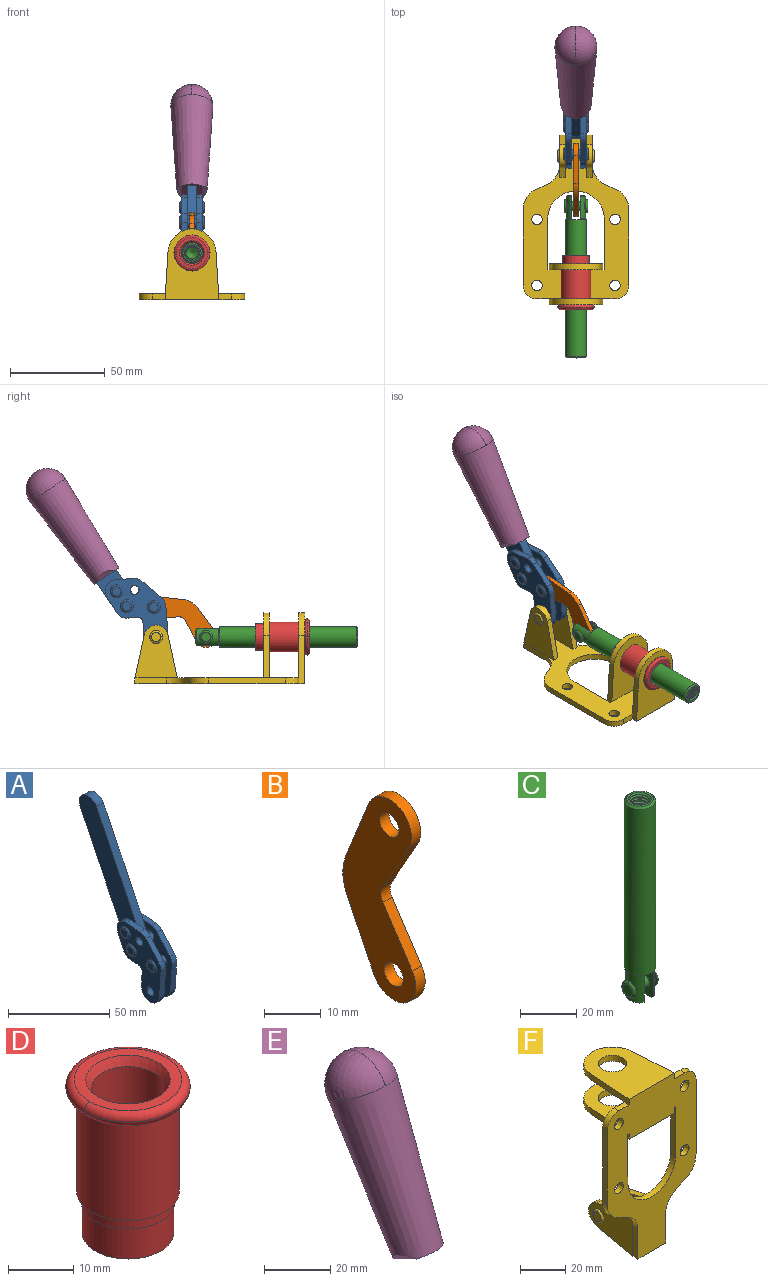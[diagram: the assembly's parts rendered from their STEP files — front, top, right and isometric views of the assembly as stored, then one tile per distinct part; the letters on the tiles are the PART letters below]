
ASSEMBLY  parts=6 mates=6
PART A: 59 faces, bbox 12.9x60.2x99.6 mm
  f0: torus R=2.39mm, axis (-1,0,0), area 14.9mm2, adj f20,f43,f51
  f1: torus R=2.39mm, axis (-1,0,0), area 14.9mm2, adj f19,f42,f51
  f2: torus R=2.39mm, axis (-1,0,0), area 14.9mm2, adj f18,f35,f51
  f3: torus R=2.39mm, axis (-1,0,0), area 14.9mm2, adj f14,f17,f23
  f4: torus R=2.39mm, axis (-1,0,0), area 14.9mm2, adj f13,f16,f23
  f5: torus R=2.39mm, axis (-1,0,0), area 14.9mm2, adj f12,f15,f23
  f6: cylinder r=2.39mm len=4.78mm, axis (1,0,0), area 46.5mm2, adj f48,f50,f51
  f7: cylinder r=2.39mm len=4.78mm, axis (1,0,0), area 46.5mm2, adj f50,f51
  f8: cylinder r=6.35mm len=12.68mm, axis (1,0,0), area 61.8mm2, adj f38,f39,f50,f51
  f9: cylinder r=2.39mm len=4.78mm, axis (-1,0,0), area 70.5mm2, adj f46,f50
  f10: cylinder r=2.39mm len=4.78mm, axis (-1,0,0), area 46.5mm2, adj f23,f45,f46
  f11: cylinder r=2.39mm len=4.78mm, axis (-1,0,0), area 46.5mm2, adj f23,f46
  f12: plane 4.78x4.78mm, normal (1,0,0), area 17.9mm2, adj f5,f15
  f13: plane 4.78x4.78mm, normal (1,0,0), area 17.9mm2, adj f4,f16
  f14: plane 4.78x4.78mm, normal (1,0,0), area 17.9mm2, adj f3,f17
  f15: torus R=2.39mm, axis (-1,0,0), area 14.9mm2, adj f5,f12,f23
  f16: torus R=2.39mm, axis (-1,0,0), area 14.9mm2, adj f4,f13,f23
  f17: torus R=2.39mm, axis (-1,0,0), area 14.9mm2, adj f3,f14,f23
  f18: plane 4.78x4.78mm, normal (-1,0,0), area 17.9mm2, adj f2,f35
  f19: plane 4.78x4.78mm, normal (-1,0,0), area 17.9mm2, adj f1,f42
  f20: plane 4.78x4.78mm, normal (-1,0,0), area 17.9mm2, adj f0,f43
  f21: plane 2.26x0.2mm, normal (1,0,0), area 0.2mm2, adj f31,f44
  f22: plane 2.26x0.2mm, normal (-1,0,0), area 0.2mm2, adj f41,f44
  f23: plane 39.37x30.77mm, normal (1,0,0), area 565.5mm2, adj f3,f4,f5,f10,f11,f15,f16,f17
  f24: cylinder r=6.1mm len=4.15mm, axis (-1,0,0), area 14.7mm2, adj f23,f25,f32,f46
  f25: plane 10.25x9.01mm, normal (0,-0.75,0.66), area 42.3mm2, adj f23,f24,f26,f46
  f26: cylinder r=6.35mm len=4.64mm, axis (-1,0,0), area 15.6mm2, adj f23,f25,f27,f46
  f27: plane 15.84x3.1mm, normal (0,-1,-0.07), area 49.2mm2, adj f23,f26,f28,f46
  f28: cylinder r=6.35mm len=12.68mm, axis (-1,0,0), area 61.8mm2, adj f23,f27,f29,f46
  f29: plane 8.11x3.1mm, normal (0,1,0.07), area 25.2mm2, adj f23,f28,f30,f46
  f30: cylinder r=3.05mm len=3.25mm, axis (-1,0,0), area 14.8mm2, adj f23,f29,f31,f46
  f31: plane 5.99x3.1mm, normal (0,0.07,-1), area 18.6mm2, adj f21,f23,f30,f44,f46
  f32: plane 9.5x3.1mm, normal (0,-0.07,1), area 29.5mm2, adj f23,f24,f33,f46,f47
  f33: cylinder r=6.1mm len=8.63mm, axis (-1,0,0), area 39.1mm2, adj f23,f32,f34,f47
  f34: plane 8.65x3.96mm, normal (0,0.91,-0.42), area 29.5mm2, adj f23,f33,f44,f47
  f35: torus R=2.39mm, axis (-1,0,0), area 14.9mm2, adj f2,f18,f51
  f36: plane 10.25x9.01mm, normal (0,-0.75,0.66), area 42.3mm2, adj f37,f49,f50,f51
  f37: cylinder r=6.35mm len=4.64mm, axis (1,0,0), area 15.6mm2, adj f36,f38,f50,f51
  f38: plane 15.84x3.1mm, normal (0,-1,-0.07), area 49.2mm2, adj f8,f37,f50,f51
  f39: plane 8.11x3.1mm, normal (0,1,0.07), area 25.2mm2, adj f8,f40,f50,f51
  f40: cylinder r=3.05mm len=3.25mm, axis (1,0,0), area 14.8mm2, adj f39,f41,f50,f51
  f41: plane 5.99x3.1mm, normal (0,0.07,-1), area 18.6mm2, adj f22,f40,f44,f50,f51
  f42: torus R=2.39mm, axis (-1,0,0), area 14.9mm2, adj f1,f19,f51
  f43: torus R=2.39mm, axis (-1,0,0), area 14.9mm2, adj f0,f20,f51
  f44: cylinder r=6.35mm len=12.12mm, axis (-1,0,0), area 128.9mm2, adj f21,f22,f23,f31,f34,f41,f46,f47
  f45: plane 2.65x1.35mm, normal (1,0,0), area 1mm2, adj f10,f55
  f46: plane 39.08x20.42mm, normal (-1,0,0), area 412.5mm2, adj f9,f10,f11,f24,f25,f26,f27,f28
  f47: plane 77.62x39.82mm, normal (1,0,0), area 850mm2, adj f32,f33,f34,f44,f53,f54,f55
  f48: plane 2.65x1.35mm, normal (-1,0,0), area 1mm2, adj f6,f55
  f49: cylinder r=6.1mm len=4.15mm, axis (1,0,0), area 14.7mm2, adj f36,f50,f51,f56
  f50: plane 39.08x20.42mm, normal (1,0,0), area 412.5mm2, adj f6,f7,f8,f9,f36,f37,f38,f39
  f51: plane 39.37x30.77mm, normal (-1,0,0), area 565.5mm2, adj f0,f1,f2,f6,f7,f8,f35,f36
  f52: plane 8.65x3.96mm, normal (0,0.91,-0.42), area 29.5mm2, adj f44,f51,f57,f58
  f53: plane 68.49x33.4mm, normal (0,0.9,-0.44), area 358.1mm2, adj f44,f47,f54,f58
  f54: cylinder r=6.35mm len=12.06mm, axis (1,0,0), area 93.7mm2, adj f47,f53,f55,f58
  f55: plane 68.49x33.4mm, normal (0,-0.9,0.44), area 358.1mm2, adj f44,f45,f46,f47,f48,f50,f54,f58
  f56: plane 9.5x3.1mm, normal (0,-0.07,1), area 29.5mm2, adj f49,f50,f51,f57,f58
  f57: cylinder r=6.1mm len=8.63mm, axis (1,0,0), area 39.1mm2, adj f51,f52,f56,f58
  f58: plane 77.62x39.82mm, normal (-1,0,0), area 850mm2, adj f44,f52,f53,f54,f55,f56,f57
PART B: 12 faces, bbox 2.3x18.2x42.8 mm
  f0: cylinder r=2.4mm len=4.8mm, axis (1,0,0), area 34.9mm2, adj f4,f11
  f1: cylinder r=10.41mm len=8.47mm, axis (1,0,0), area 20.2mm2, adj f4,f9,f10,f11
  f2: cylinder r=3.05mm len=3.16mm, axis (1,0,0), area 7.7mm2, adj f4,f6,f7,f11
  f3: cylinder r=2.4mm len=4.8mm, axis (1,0,0), area 34.9mm2, adj f4,f11
  f4: plane 42.81x18.23mm, normal (-1,0,0), area 414.1mm2, adj f0,f1,f2,f3,f5,f6,f7,f8
  f5: cylinder r=5.54mm len=10.67mm, axis (1,0,0), area 41.8mm2, adj f4,f6,f10,f11
  f6: plane 11.66x6.53mm, normal (0,-0.87,-0.49), area 30.9mm2, adj f2,f4,f5,f11
  f7: plane 11.17x7.33mm, normal (0,-0.84,0.55), area 30.9mm2, adj f2,f4,f8,f11
  f8: cylinder r=5.54mm len=10.51mm, axis (1,0,0), area 41.8mm2, adj f4,f7,f9,f11
  f9: plane 13.67x6.67mm, normal (0,0.9,-0.44), area 35.1mm2, adj f1,f4,f8,f11
  f10: plane 14.1x5.7mm, normal (0,0.93,0.37), area 35.1mm2, adj f1,f4,f5,f11
  f11: plane 42.81x18.23mm, normal (1,0,0), area 414.1mm2, adj f0,f1,f2,f3,f5,f6,f7,f8
PART C: 48 faces, bbox 12.6x11.1x86.1 mm
  f0: torus R=2.41mm, axis (-1,0,0), area 15mm2, adj f30,f32,f34
  f1: torus R=2.41mm, axis (-1,0,0), area 15mm2, adj f29,f31,f33
  f2: cylinder r=5.54mm len=72.39mm, axis (0,0,1), area 2518.5mm2, adj f3,f4,f42,f43
  f3: cone r=5.54mm half-angle=45deg, axis (0,0,1), area 7.6mm2, adj f2,f5,f41
  f4: cone r=5.54mm half-angle=45deg, axis (0,0,-1), area 34.9mm2, adj f2,f39
  f5: cylinder r=5.08mm len=11.48mm, axis (0,0,1), area 108.3mm2, adj f3,f7,f8,f41
  f6: cylinder r=2.41mm len=4.83mm, axis (-1,0,0), area 71.2mm2, adj f40,f41
  f7: cylinder r=2.41mm len=4.83mm, axis (-1,0,0), area 7.6mm2, adj f5,f34
  f8: cone r=5.08mm half-angle=45deg, axis (0,0,1), area 10.6mm2, adj f5,f37,f41
  f9: cone r=3.98mm half-angle=45deg, axis (0,0,1), area 17.6mm2, adj f27,f39,f45,f46,f47
  f10: cylinder r=2.41mm len=4.83mm, axis (-1,0,0), area 7.6mm2, adj f33,f38
  f11: cylinder r=3.2mm len=6.4mm, axis (0,0,1), area 78.4mm2, adj f12,f28,f44,f45,f47
  f12: cylinder r=3.2mm len=6.4mm, axis (0,0,1), area 10.5mm2, adj f11,f13,f45,f47
  f13: cylinder r=3.2mm len=6.4mm, axis (0,0,1), area 10.5mm2, adj f12,f14,f45,f47
  f14: cylinder r=3.2mm len=6.4mm, axis (0,0,1), area 10.5mm2, adj f13,f15,f45,f47
  f15: cylinder r=3.2mm len=6.4mm, axis (0,0,1), area 10.5mm2, adj f14,f16,f45,f47
  f16: cylinder r=3.2mm len=6.4mm, axis (0,0,1), area 10.5mm2, adj f15,f17,f45,f47
  f17: cylinder r=3.2mm len=6.4mm, axis (0,0,1), area 10.5mm2, adj f16,f18,f45,f47
  f18: cylinder r=3.2mm len=6.4mm, axis (0,0,1), area 10.5mm2, adj f17,f19,f45,f47
  f19: cylinder r=3.2mm len=6.4mm, axis (0,0,1), area 10.5mm2, adj f18,f20,f45,f47
  f20: cylinder r=3.2mm len=6.4mm, axis (0,0,1), area 10.5mm2, adj f19,f21,f45,f47
  f21: cylinder r=3.2mm len=6.4mm, axis (0,0,1), area 10.5mm2, adj f20,f22,f45,f47
  f22: cylinder r=3.2mm len=6.4mm, axis (0,0,1), area 10.5mm2, adj f21,f23,f45,f47
  f23: cylinder r=3.2mm len=6.4mm, axis (0,0,1), area 10.5mm2, adj f22,f24,f45,f47
  f24: cylinder r=3.2mm len=6.4mm, axis (0,0,1), area 10.5mm2, adj f23,f25,f45,f47
  f25: cylinder r=3.2mm len=6.4mm, axis (0,0,1), area 10.5mm2, adj f24,f26,f45,f47
  f26: cylinder r=3.2mm len=6.4mm, axis (0,0,1), area 10.5mm2, adj f25,f27,f45,f47
  f27: cylinder r=3.2mm len=6.4mm, axis (0,0,1), area 7.4mm2, adj f9,f26,f45,f47
  f28: cone r=3.2mm half-angle=60deg, axis (0,0,1), area 37.2mm2, adj f11
  f29: plane 4.83x4.83mm, normal (-1,0,0), area 18.3mm2, adj f1,f31
  f30: plane 4.83x4.83mm, normal (1,0,0), area 18.3mm2, adj f0,f32
  f31: torus R=2.41mm, axis (-1,0,0), area 15mm2, adj f1,f29,f33
  f32: torus R=2.41mm, axis (-1,0,0), area 15mm2, adj f0,f30,f34
  f33: plane 6.83x6.83mm, normal (1,0,0), area 18.3mm2, adj f1,f10,f31
  f34: plane 6.83x6.83mm, normal (-1,0,0), area 18.3mm2, adj f0,f7,f32
  f35: cone r=5.08mm half-angle=45deg, axis (0,0,1), area 10.6mm2, adj f36,f38,f40
  f36: plane 7.25x1.97mm, normal (0,0,-1), area 10mm2, adj f35,f40
  f37: plane 7.25x1.97mm, normal (0,0,-1), area 10mm2, adj f8,f41
  f38: cylinder r=5.08mm len=11.48mm, axis (0,0,1), area 108.3mm2, adj f10,f35,f40,f42
  f39: plane 9.55x9.55mm, normal (0,0,1), area 22mm2, adj f4,f9
  f40: plane 12.76x10.09mm, normal (1,0,0), area 95.7mm2, adj f6,f35,f36,f38,f42,f43
  f41: plane 12.76x10.09mm, normal (-1,0,0), area 95.7mm2, adj f3,f5,f6,f8,f37,f43
  f42: cone r=5.54mm half-angle=45deg, axis (0,0,1), area 7.6mm2, adj f2,f38,f40
  f43: plane 11.07x4.7mm, normal (0,0,-1), area 50.4mm2, adj f2,f40,f41
  f44: plane 0.89x0.62mm, normal (-1,0,0), area 0.3mm2, adj f11,f45,f46,f47
  f45: bspline ~24.8x7.63mm, area 266.6mm2, adj f9,f11,f12,f13,f14,f15,f16,f17
  f46: bspline ~24.87x7.63mm, area 73.6mm2, adj f9,f44,f45,f47
  f47: bspline ~24.98x7.63mm, area 272.5mm2, adj f9,f11,f12,f13,f14,f15,f16,f17
PART D: 15 faces, bbox 20.6x20.6x28.7 mm
  f0: torus R=8.26mm, axis (0,0,1), area 56.8mm2, adj f1,f10,f12
  f1: torus R=8.26mm, axis (0,0,1), area 56.8mm2, adj f0,f6,f13
  f2: cylinder r=5.59mm len=25.91mm, axis (0,0,1), area 909.6mm2, adj f3,f4
  f3: cone r=6.86mm half-angle=45deg, axis (0,0,-1), area 70.2mm2, adj f2,f14
  f4: cone r=6.47mm half-angle=30deg, axis (0,0,1), area 66.7mm2, adj f2,f13
  f5: cylinder r=7.04mm len=14.07mm, axis (0,0,1), area 252.6mm2, adj f11,f14
  f6: torus R=8.26mm, axis (0,0,1), area 56.8mm2, adj f1,f12,f13
  f7: cylinder r=7.16mm len=14.33mm, axis (0,0,1), area 91.5mm2, adj f9,f11
  f8: cylinder r=7.86mm len=18.42mm, axis (0,0,1), area 909.6mm2, adj f9,f10
  f9: plane 15.72x15.72mm, normal (0,0,-1), area 33mm2, adj f7,f8
  f10: plane 16.51x16.51mm, normal (0,0,-1), area 19.9mm2, adj f0,f8,f12
  f11: plane 14.33x14.33mm, normal (0,0,-1), area 5.7mm2, adj f5,f7
  f12: torus R=8.26mm, axis (0,0,1), area 56.8mm2, adj f0,f6,f10
  f13: plane 16.51x16.51mm, normal (0,0,1), area 82.7mm2, adj f1,f4,f6
  f14: plane 14.07x14.07mm, normal (0,0,-1), area 7.8mm2, adj f3,f5
PART E: 11 faces, bbox 22.3x42.6x64.5 mm
  f0: sphere r=11.13mm, area 411.4mm2, adj f1,f8
  f1: cone r=11.11mm half-angle=3.3deg, axis (0,0.44,0.9), area 3251.8mm2, adj f0,f7,f8,f9,f10
  f2: cylinder r=6.16mm len=11.7mm, axis (1,0,0), area 89.5mm2, adj f3,f4,f5,f6
  f3: plane 60.23x36.75mm, normal (-1,0,0), area 763.6mm2, adj f2,f4,f6,f10
  f4: plane 51.37x25.05mm, normal (0,0.9,-0.44), area 264.2mm2, adj f2,f3,f5,f10
  f5: plane 60.23x36.75mm, normal (1,0,0), area 763.6mm2, adj f2,f4,f6,f10
  f6: plane 51.37x25.05mm, normal (0,-0.9,0.44), area 264.2mm2, adj f2,f3,f5,f10
  f7: plane 9.95x5.95mm, normal (0.71,-0.31,-0.64), area 25.8mm2, adj f1,f10
  f8: sphere r=11.13mm, area 411.4mm2, adj f0,f1
  f9: plane 9.95x5.95mm, normal (-0.71,-0.31,-0.64), area 25.8mm2, adj f1,f10
  f10: plane 14.27x11.38mm, normal (0,-0.44,-0.9), area 106.7mm2, adj f1,f3,f4,f5,f6,f7,f9
PART F: 55 faces, bbox 55.7x37.4x89.8 mm
  f0: torus R=2.41mm, axis (-1,0,0), area 15mm2, adj f11,f15,f25
  f1: torus R=2.41mm, axis (-1,0,0), area 15mm2, adj f10,f12,f22
  f2: cylinder r=2.78mm len=5.56mm, axis (0,-1,0), area 54.2mm2, adj f30,f54
  f3: cylinder r=14.99mm len=29.97mm, axis (0,-1,0), area 145.9mm2, adj f30,f49,f53,f54
  f4: cylinder r=2.78mm len=5.56mm, axis (0,-1,0), area 54.2mm2, adj f30,f54
  f5: cylinder r=2.78mm len=5.56mm, axis (0,-1,0), area 54.2mm2, adj f30,f54
  f6: cylinder r=2.78mm len=5.56mm, axis (0,-1,0), area 54.2mm2, adj f30,f54
  f7: cylinder r=6.35mm len=12.7mm, axis (0,0,1), area 123.6mm2, adj f27,f51
  f8: cylinder r=6.35mm len=12.7mm, axis (0,0,-1), area 124.7mm2, adj f21,f35
  f9: cylinder r=2.41mm len=11.18mm, axis (-1,0,0), area 169.4mm2, adj f16,f19
  f10: plane 4.83x4.83mm, normal (1,0,0), area 18.3mm2, adj f1,f12
  f11: plane 4.83x4.83mm, normal (-1,0,0), area 18.3mm2, adj f0,f15
  f12: torus R=2.41mm, axis (-1,0,0), area 15mm2, adj f1,f10,f22
  f13: cylinder r=6.35mm len=12.41mm, axis (1,0,0), area 53.4mm2, adj f18,f19,f22,f23
  f14: cylinder r=6.35mm len=12.41mm, axis (-1,0,0), area 53.4mm2, adj f16,f17,f24,f25
  f15: torus R=2.41mm, axis (-1,0,0), area 15mm2, adj f0,f11,f25
  f16: plane 27.86x22.35mm, normal (1,0,0), area 425.4mm2, adj f9,f14,f17,f24,f30
  f17: plane 22.86x4.97mm, normal (0,0.21,0.98), area 72.5mm2, adj f14,f16,f25,f30
  f18: plane 22.86x4.97mm, normal (0,0.21,0.98), area 72.5mm2, adj f13,f19,f22,f30
  f19: plane 27.86x22.35mm, normal (-1,0,0), area 425.4mm2, adj f9,f13,f18,f23,f30
  f20: cylinder r=12.7mm len=25.35mm, axis (0,0,-1), area 119.8mm2, adj f21,f34,f35,f36
  f21: plane 34.21x28.07mm, normal (0,0,-1), area 702.4mm2, adj f8,f20,f30,f34,f36
  f22: plane 27.96x22.45mm, normal (1,0,0), area 407.2mm2, adj f1,f12,f13,f18,f23,f30,f42,f43
  f23: plane 22.86x4.97mm, normal (0,0.21,-0.98), area 72.5mm2, adj f13,f19,f22,f44
  f24: plane 22.86x4.97mm, normal (0,0.21,-0.98), area 72.5mm2, adj f14,f16,f25,f44
  f25: plane 27.86x22.35mm, normal (-1,0,0), area 407.1mm2, adj f0,f14,f15,f17,f24,f30,f45,f46
  f26: plane 3.1x0.95mm, normal (0,0,-1), area 2.7mm2, adj f30,f49,f50,f54
  f27: plane 34.21x28.07mm, normal (0,0,1), area 702.4mm2, adj f7,f28,f30,f50,f52
  f28: cylinder r=12.7mm len=25.35mm, axis (0,0,1), area 118.8mm2, adj f27,f50,f51,f52
  f29: plane 3.1x0.95mm, normal (0,0,-1), area 2.7mm2, adj f30,f52,f53,f54
  f30: plane 86.54x55.63mm, normal (0,1,0), area 2362.9mm2, adj f2,f3,f4,f5,f6,f16,f17,f18
  f31: plane 40.56x3.1mm, normal (-1,0,0), area 125.7mm2, adj f30,f32,f48,f54
  f32: cylinder r=7.11mm len=7.11mm, axis (0,-1,0), area 34.6mm2, adj f30,f31,f33,f54
  f33: plane 6.67x3.1mm, normal (0,0,1), area 20.4mm2, adj f30,f32,f34,f54
  f34: plane 25.39x3.13mm, normal (-1,0.06,0), area 79.5mm2, adj f20,f21,f33,f35,f54
  f35: plane 37.31x28.45mm, normal (0,0,1), area 789.9mm2, adj f8,f20,f34,f36,f54
  f36: plane 25.39x3.13mm, normal (1,0.06,0), area 79.5mm2, adj f20,f21,f35,f37,f54
  f37: plane 6.67x3.1mm, normal (0,0,1), area 20.4mm2, adj f30,f36,f38,f54
  f38: cylinder r=7.11mm len=7.11mm, axis (0,-1,0), area 34.6mm2, adj f30,f37,f39,f54
  f39: plane 40.56x3.1mm, normal (1,0,0), area 125.7mm2, adj f30,f38,f40,f54
  f40: cylinder r=11.18mm len=10.16mm, axis (0,-1,0), area 39.5mm2, adj f30,f39,f41,f54
  f41: plane 6.09x3.1mm, normal (0.42,0,-0.91), area 20.8mm2, adj f30,f40,f42,f54
  f42: cylinder r=11.18mm len=9.41mm, axis (0,-1,0), area 37.2mm2, adj f22,f30,f41,f43,f54
  f43: plane 16.5x3.1mm, normal (1,0,0), area 51.1mm2, adj f22,f42,f44,f54
  f44: plane 17.37x3.1mm, normal (0,0,-1), area 53.8mm2, adj f23,f24,f30,f43,f45,f54
  f45: plane 16.5x3.1mm, normal (-1,0,0), area 51.1mm2, adj f25,f44,f46,f54
  f46: cylinder r=11.18mm len=9.41mm, axis (0,-1,0), area 37.2mm2, adj f25,f30,f45,f47,f54
  f47: plane 6.09x3.1mm, normal (-0.42,0,-0.91), area 20.8mm2, adj f30,f46,f48,f54
  f48: cylinder r=11.18mm len=10.16mm, axis (0,-1,0), area 39.5mm2, adj f30,f31,f47,f54
  f49: plane 26.54x3.1mm, normal (-1,0,0), area 82.3mm2, adj f3,f26,f30,f54
  f50: plane 25.39x3.1mm, normal (1,0.06,0), area 78.8mm2, adj f26,f27,f28,f51,f54
  f51: plane 37.31x28.45mm, normal (0,0,-1), area 789.9mm2, adj f7,f28,f50,f52,f54
  f52: plane 25.39x3.1mm, normal (-1,0.06,0), area 78.8mm2, adj f27,f28,f29,f51,f54
  f53: plane 26.54x3.1mm, normal (1,0,0), area 82.3mm2, adj f3,f29,f30,f54
  f54: plane 89.66x55.63mm, normal (0,-1,0), area 2678.5mm2, adj f2,f3,f4,f5,f6,f26,f29,f31
PLACE A rot(axis=(-1,0,0),8.3deg) t=(0,21.5,59.92)mm
PLACE B rot(axis=(1,0,0),121.9deg) t=(0,41.04,11.9)mm
PLACE C rot(axis=(1,0,0),90deg) t=(0,30.37,0)mm
PLACE D rot(axis=(1,0,0),90deg) t=(0,9.14,0)mm
PLACE E rot(axis=(-1,0,0),8.3deg) t=(-0.04,21.5,59.92)mm
PLACE F rot(axis=(1,0,0),90deg) t=(0,9.14,0)mm fixed
MATE fastened D.f0 <-> F.f7  axis (0,1,0) through (0,-37.25,24.61)mm
MATE fastened E.f2 <-> A.f54  axis (1,0,0) through (-2.35,99.7,103.88)mm
MATE revolute C.f6 <-> B.f5  axis (-1,0,0) through (0,14.9,24.61)mm
MATE revolute B.f3 <-> A.f4  axis (1,0,0) through (0,42.42,40.44)mm
MATE slider C.f2 <-> F.f7  axis (0,-1,0) through (0,-28.41,24.61)mm
MATE revolute F.f0 <-> A.f7  axis (-1,0,0) through (0,41.23,24.61)mm
